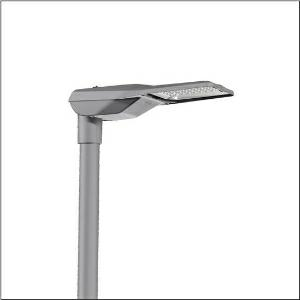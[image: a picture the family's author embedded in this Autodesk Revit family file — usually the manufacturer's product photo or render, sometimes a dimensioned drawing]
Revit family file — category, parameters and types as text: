
# Revit family: streetlight_sl_21_mini___st0_5a_5xe2b43s08gb_d1ce
name_source: partatom
category: Lighting Fixtures
units: mm (PartAtom-declared; Revit-internal decimal feet)

## family parameters
Cut with Voids When Loaded = No
Host = Face
Light Source = No
Part Type = Normal
Room Calculation Point = No
Round Connector Dimension = Use Diameter
Shared = No

## types (1)
- --- (1 x LED, 6180 lm, 40.4 W, 4000K)
    Apparent Load = 40 VA
    CIE Flux Codes = 41 75 97 100 100
    Color Rendering = 70
    Color Temperature = 4000K
    Default Elevation = 1800 mm
    Description = Streetlight SL 21 mini, mast luminaire, primary light control with lens, of PMMA, primary optical cover: cover, of toughened safety glass, transparent, light distribution: ST0.5a, light emission: direct distribution, primary light characteristic: asymmetric, installation type: side-entry, post-top, LED, High Power LED, rated luminous flux: 6.180lm, luminous efficacy: 153lm/W, light colour: 740, colour temperature: 4000K, control gear: D4i, control: overheat protection, constant luminous flux control, time-dependent luminous flux control, flexible luminous flux parameterisation, pre-setting: logarithmic dimming characteristic, mains connection: 220..240V, AC, 50/60Hz, start of lifetime: 40W, end of service life: 41W, reduction: 19W, luminaire housing, of diecast aluminium, powder-coated, SITECO metallic grey (DB 702S), corrosivity category C5 high according to DIN EN ISO 12944, please order mast flange separately, inclination adjustable: 0°, 5°, 10°, 15°, sealing non-destructively replaceable, multi-level sealing system, length: 628mm, width: 235mm, height: 110mm, mast flange for spigot size: 42mm (side-entry): 5XC10008XM4, 60/48mm (side-entry/post-top): 5XC10108XM2, 76/60mm (side-entry/post-top): 5XC10108XM1, mounting height: 4..8m, Smart Interface above, protection rating (complete): IP66, insulation class (complete): insulation class II (safety insulation), certification: CE, ENEC, ENEC+, VDE, impact resistance: IK10, permissible operating ambient temperature for outdoor applications: -40..+50°C, standard-compliant lighting for roads and squares, packaging unit: 1 piece

Light Distribution: ST0.5a
    Height = 110 mm
    Lamp = 1 x LED
    Lamp Light Flux = 6180 lm
    Lamp Power = 40.4 W
    Lamp count = 1
    Length = 625 mm
    Luminous efficacy = 153 lm/W
    Manufacturer = Siteco
    ModVariant = No
    Model = 5XE2B43S08GB
    Number of Poles = 1
    OnlyDefault = Yes
    Power Factor = 1
    Product Name = Streetlight SL 21 mini | ST0.5a
    Product group = mast luminaire | pylon top
    ProductGroupID = 6100
    Protection Class = Protection class II
    Protection Degree = IP 66
    RLX_Detail_Level = 1
    RLX_Emergency_Light_Flux = 0 lm
    RLX_Emergency_Type = 0
    RLX_Emergency_Type_DB = No
    RlxData = <blob elided: 37113 chars, md5=407c7e2b>
    Socket = socket
    Standby Power = 0 W
    System Light Flux = 6180 lm
    System Power = 40 W
    Type Comments = factory setting: luminous flux: 100 % | dim-lin: 254 | 812 mA
    Type Image = l_1003515.jpg
    URL = http://relux.com
    VarID = @adj_188687
    Voltage = 0 V
    Weight = 0.00 kg
    Width = 234 mm

## geometry (parser evidence)
native form markers: Blend x4, Sweep x11
no freeform markers — native parametric forms only
